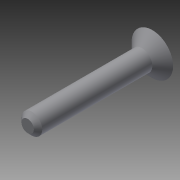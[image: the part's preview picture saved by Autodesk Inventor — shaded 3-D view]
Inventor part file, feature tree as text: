
AUTODESK INVENTOR PART (.ipt)
format: ipt  version: 2013 (Build 170138000, 138)  size: 95,232 bytes
history: native  units: mm
features: sketch x2, revolve x1, extrude x1
ambient origin geometry x8: Origin, YZ Plane, XZ Plane, XY Plane, X Axis, Y Axis, Z Axis, Center Point
bodies: Solid1 (feature_tree)
feature tree (4):
  revolve  "Revolution1"  [1 undecoded]
  extrude  "Extrusion1"  Depth=30.0mm
  sketch  "Sketch1"  dims[d0=2.5mm d2=5.0mm]
  sketch  "Sketch2"  dims[d3=135.0deg d4=30.0mm d5=90.0deg d6=1.0mm d7=1.0mm d8=3.0mm d9=2.0mm d10=0.0mm]
note: 1 required parameter value undecoded (feature->parameter linkage not recoverable at this tier; creation-order binding heuristic only, values carry confidence <= 0.55)
